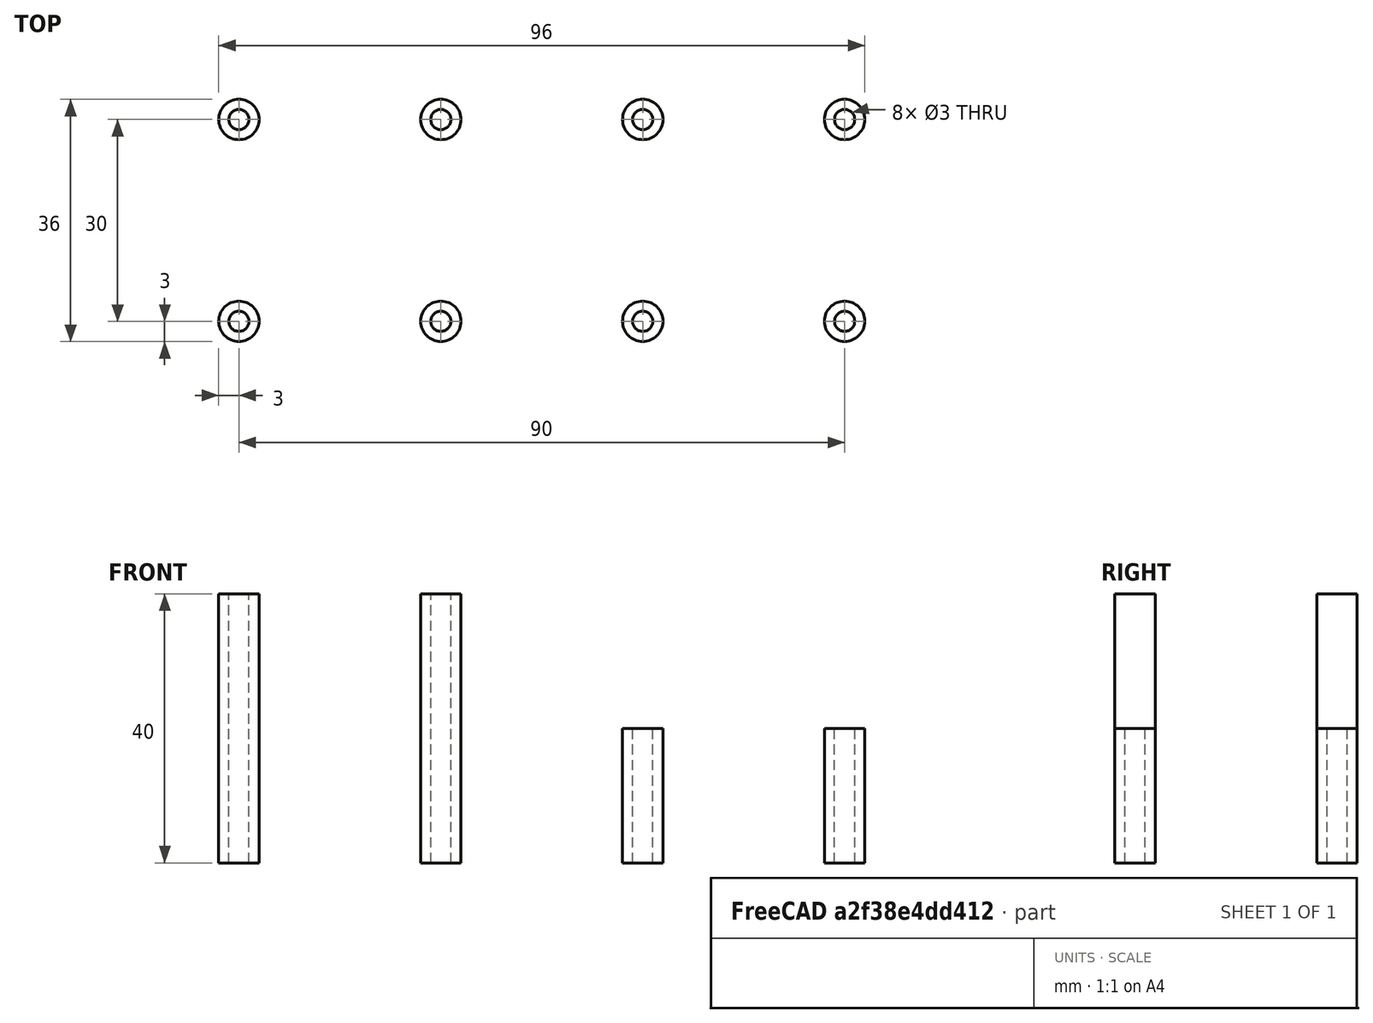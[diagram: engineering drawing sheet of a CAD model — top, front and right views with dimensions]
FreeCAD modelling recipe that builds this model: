
FCSTD DOCUMENT  (FreeCAD 0.17R13541 (Git))
Label: poles
License: All rights reserved
LicenseURL: http://en.wikipedia.org/wiki/All_rights_reserved
objects: Part::Cylinder×16, Part::Cut×8
note: 24 computed .brp shape members not serialized (recipe doc carries the construction recipe); baked Part::Feature solids carry a one-line shape summary decoded from their .brp

FEATURE [Part::Cylinder] Cylinder
  Angle = 360
  AttacherType = Attacher::AttachEngine3D
  Height = 40
  Radius = 3
FEATURE [Part::Cylinder] Cylinder001
  Angle = 360
  AttacherType = Attacher::AttachEngine3D
  Height = 40
  Radius = 1.5
FEATURE [Part::Cylinder] Cylinder008
  Angle = 360
  AttacherType = Attacher::AttachEngine3D
  Height = 20
  Placement = pos=(60,0,0) rot=(0,0,1;0rad)
  Radius = 1.5
FEATURE [Part::Cylinder] Cylinder009
  Angle = 360
  AttacherType = Attacher::AttachEngine3D
  Height = 20
  Placement = pos=(60,0,0) rot=(0,0,1;0rad)
  Radius = 3
FEATURE [Part::Cut] Cut001  label="20mm 1"
  Base = -> Cylinder009
  Tool = -> Cylinder008
FEATURE [Part::Cut] Cut  label="40mm 1"
  Base = -> Cylinder
  Tool = -> Cylinder001
FEATURE [Part::Cylinder] Cylinder010
  Angle = 360
  AttacherType = Attacher::AttachEngine3D
  Height = 40
  Radius = 3
FEATURE [Part::Cylinder] Cylinder011
  Angle = 360
  AttacherType = Attacher::AttachEngine3D
  Height = 40
  Radius = 1.5
FEATURE [Part::Cut] Cut002  label="40mm 2"
  Base = -> Cylinder010
  Placement = pos=(30,0,0) rot=(0,0,1;0rad)
  Tool = -> Cylinder011
FEATURE [Part::Cylinder] Cylinder012
  Angle = 360
  AttacherType = Attacher::AttachEngine3D
  Height = 40
  Radius = 3
FEATURE [Part::Cylinder] Cylinder013
  Angle = 360
  AttacherType = Attacher::AttachEngine3D
  Height = 40
  Radius = 1.5
FEATURE [Part::Cut] Cut003  label="40mm 3"
  Base = -> Cylinder012
  Placement = pos=(30,30,0) rot=(0,0,1;0rad)
  Tool = -> Cylinder013
FEATURE [Part::Cylinder] Cylinder014
  Angle = 360
  AttacherType = Attacher::AttachEngine3D
  Height = 40
  Radius = 3
FEATURE [Part::Cylinder] Cylinder015
  Angle = 360
  AttacherType = Attacher::AttachEngine3D
  Height = 40
  Radius = 1.5
FEATURE [Part::Cut] Cut004  label="40mm 4"
  Base = -> Cylinder014
  Placement = pos=(0,30,0) rot=(0,0,1;0rad)
  Tool = -> Cylinder015
FEATURE [Part::Cylinder] Cylinder016
  Angle = 360
  AttacherType = Attacher::AttachEngine3D
  Height = 20
  Placement = pos=(60,0,0) rot=(0,0,1;0rad)
  Radius = 1.5
FEATURE [Part::Cylinder] Cylinder017
  Angle = 360
  AttacherType = Attacher::AttachEngine3D
  Height = 20
  Placement = pos=(60,0,0) rot=(0,0,1;0rad)
  Radius = 3
FEATURE [Part::Cut] Cut005  label="20mm 002"
  Base = -> Cylinder017
  Placement = pos=(30,0,0) rot=(0,0,1;0rad)
  Tool = -> Cylinder016
FEATURE [Part::Cylinder] Cylinder018
  Angle = 360
  AttacherType = Attacher::AttachEngine3D
  Height = 20
  Placement = pos=(60,0,0) rot=(0,0,1;0rad)
  Radius = 1.5
FEATURE [Part::Cylinder] Cylinder019
  Angle = 360
  AttacherType = Attacher::AttachEngine3D
  Height = 20
  Placement = pos=(60,0,0) rot=(0,0,1;0rad)
  Radius = 3
FEATURE [Part::Cut] Cut006  label="20mm 003"
  Base = -> Cylinder019
  Placement = pos=(30,30,0) rot=(0,0,1;0rad)
  Tool = -> Cylinder018
FEATURE [Part::Cylinder] Cylinder020
  Angle = 360
  AttacherType = Attacher::AttachEngine3D
  Height = 20
  Placement = pos=(60,0,0) rot=(0,0,1;0rad)
  Radius = 1.5
FEATURE [Part::Cylinder] Cylinder021
  Angle = 360
  AttacherType = Attacher::AttachEngine3D
  Height = 20
  Placement = pos=(60,0,0) rot=(0,0,1;0rad)
  Radius = 3
FEATURE [Part::Cut] Cut007  label="20mm 004"
  Base = -> Cylinder021
  Placement = pos=(0,30,0) rot=(0,0,1;0rad)
  Tool = -> Cylinder020
